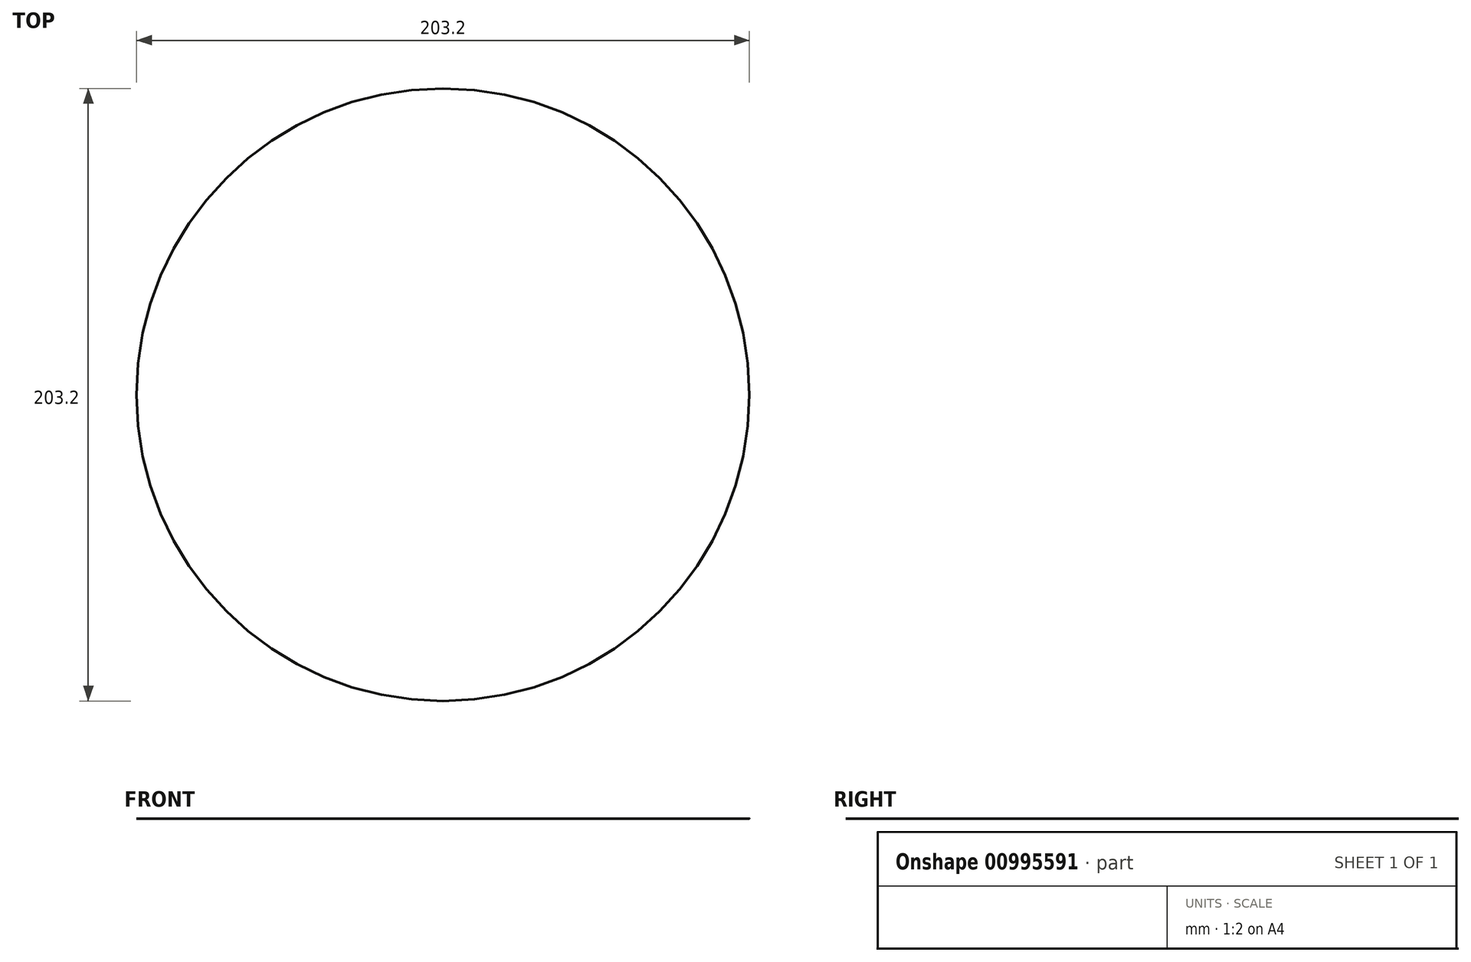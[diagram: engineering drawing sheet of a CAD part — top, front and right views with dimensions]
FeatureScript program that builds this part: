
annotation { "Feature Type Name" : "Feature", "Feature Type Description" : "" }
export const myFeature = defineFeature(function(context is Context, id is Id, definition is map)
    precondition{}
    {
        {
            var Q0;
            Q0=qCreatedBy(makeId("Top.planeOp"),FACE);
            var sketch = newSketch(context, id + "F0", { "sketchPlane" : qUnion([Q0])});
            skCircle(sketch, "E0", {"center": v(0, 0) * mm, "radius": 101.6 * mm});
            skSolve(sketch);
        }
        {
            var Q0;
            Q0 = qSketchRegion(id + "F0", true);
            extrude(context, id + "F1", {"entities" : qUnion([Q0]), "depth" : 1 / 203.2 * mm, "offsetDistance" : 25.4 * mm});
        }
        {
            var Q0;
            Q0=makeQuery(id+"F1.opExtrude","CAP_FACE",FACE,{"disambiguationData":[OSD([sQuery(id+"F0.wireOp",EDGE,"E0")])],"isStart":false});
            var sketch = newSketch(context, id + "F2", { "sketchPlane" : qUnion([Q0])});
            skPoint(sketch, "E1", {"position": v(-31.97, 45.73) * mm});
            skSolve(sketch);
        }
        {
            var Q0;
            Q0=makeQuery(id+"F2.imprint","IMPRINT",FACE,{"disambiguationData":[TD([[makeQuery(id+"F2.imprint","IMPRINT",EDGE,{"derivedFrom":makeQuery(id+"F1.opExtrude","CAP_EDGE",EDGE,{"disambiguationData":[OSD([sQuery(id+"F0.wireOp",EDGE,"E0")])],"isStart":false})}),1.0]])]});
            var sketch = newSketch(context, id + "F3", { "sketchPlane" : qUnion([Q0])});
            skCircle(sketch, "E2", {"center": v(0, 0) * mm, "radius": 19.05 * mm});
            skSolve(sketch);
        }
    });
